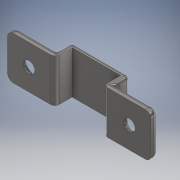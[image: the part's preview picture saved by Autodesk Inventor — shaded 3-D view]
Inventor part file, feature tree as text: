
AUTODESK INVENTOR PART (.ipt)
format: ipt  version: 2018 (Build 220112000, 112)  size: 242,176 bytes
history: native  units: mm
features: fillet x4, sketch x2, extrude x1, hole x1
ambient origin geometry x8: Origin, YZ Plane, XZ Plane, XY Plane, X Axis, Y Axis, Z Axis, Center Point
bodies: Solid1 (feature_tree)
feature tree (8):
  extrude  "Extrusion1"  Depth=16.5mm
  hole  "Hole1"  [1 undecoded]
  fillet  "Fillet1"  Radius=6.0mm
  fillet  "Fillet2"  Radius=15.0mm
  fillet  "Fillet3"  Radius=15.0mm
  fillet  "Fillet4"  Radius=2.5mm
  sketch  "Sketch1"  dims[d0=50.0mm d1=16.5mm]
  sketch  "Sketch2"  dims[d2=16.5mm d3=2.5mm d4=6.0mm d5=15.0mm d6=15.0mm d7=2.5mm d8=5.0mm d9=5.0mm d10=15.0mm d11=0.0mm d12=7.5mm d13=7.5mm d14=4.0mm d15=6.0mm d16=8.0mm d17=2.0mm d18=90.0deg d19=8.0mm d20=20.594885mm d21=1.0mm d22=1.5mm d23=2.0mm d24=1.5mm]
note: 1 required parameter value undecoded (feature->parameter linkage not recoverable at this tier; creation-order binding heuristic only, values carry confidence <= 0.55)
